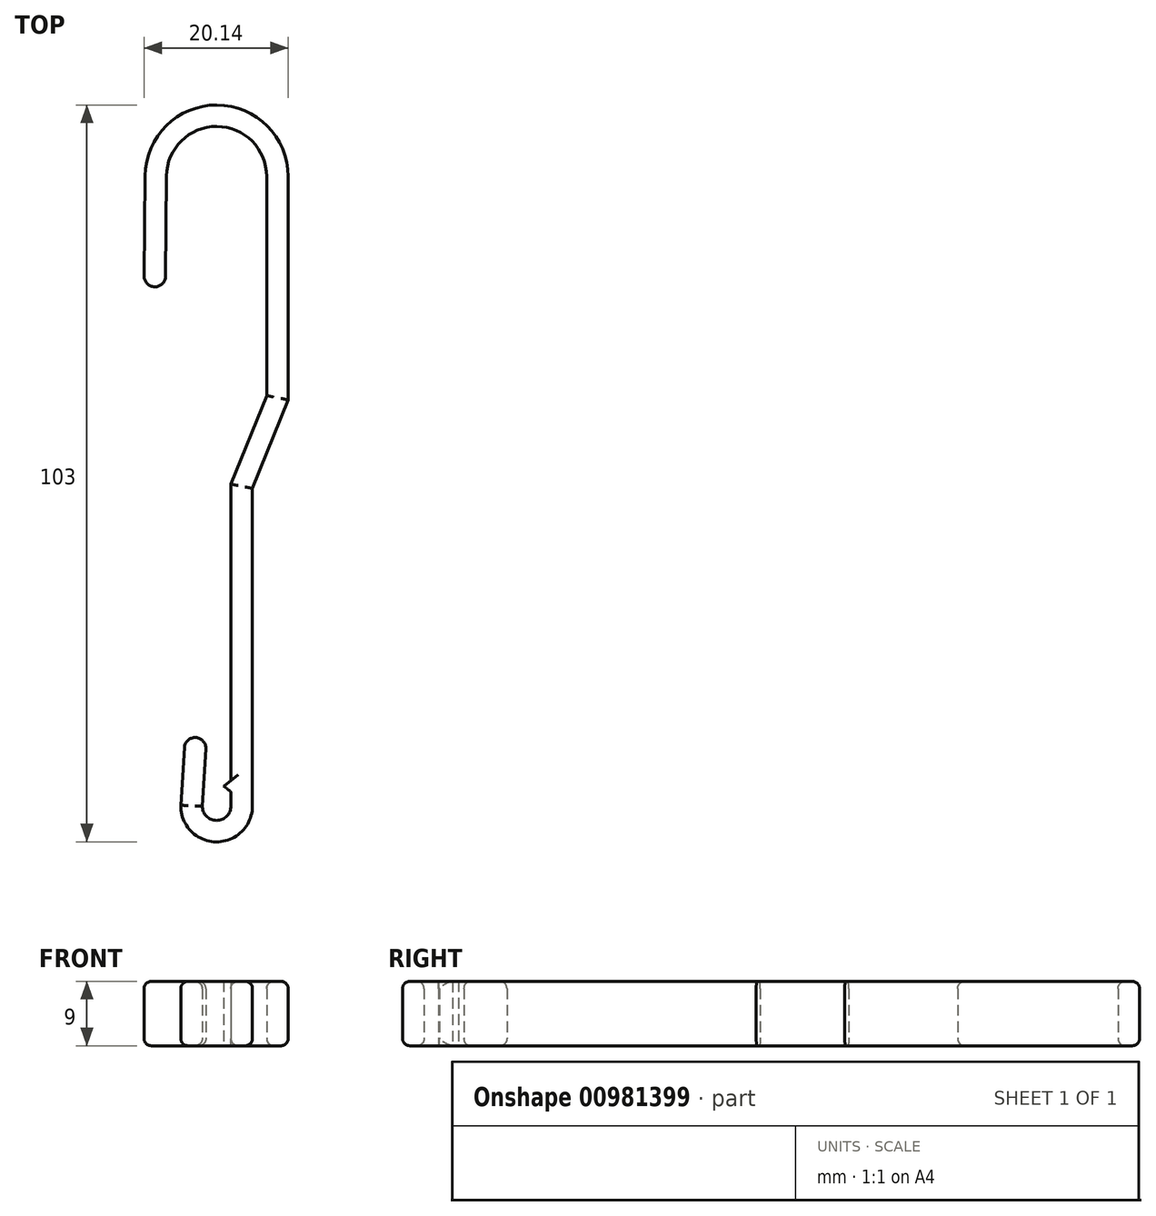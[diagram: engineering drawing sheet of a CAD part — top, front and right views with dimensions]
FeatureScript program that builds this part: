
annotation { "Feature Type Name" : "Feature", "Feature Type Description" : "" }
export const myFeature = defineFeature(function(context is Context, id is Id, definition is map)
    precondition{}
    {
        {
            var Q0;
            Q0=qCreatedBy(makeId("Top.planeOp"),FACE);
            var sketch = newSketch(context, id + "F0", { "sketchPlane" : qUnion([Q0])});
            skArc(sketch, "E0", {"start": v(-2, 0) * mm, "mid": v(0, -2) * mm, "end": v(2, 0) * mm});
            skLineSegment(sketch, "E1", {"start": v(-2, 0) * mm, "end": v(-1.5, 7.98) * mm});
            skLineSegment(sketch, "E2", {"start": v(2, 2) * mm, "end": v(1, 2.8) * mm});
            skLineSegment(sketch, "E3", {"start": v(1, 2.8) * mm, "end": v(2, 3.6) * mm});
            skLineSegment(sketch, "E4", {"start": v(2, 0) * mm, "end": v(2, 2) * mm});
            skLineSegment(sketch, "E5", {"start": v(2, 3.6) * mm, "end": v(2, 45) * mm});
            skArc(sketch, "E6", {"start": v(7, 88) * mm, "mid": v(0.03, 95) * mm, "end": v(-7, 88.07) * mm});
            skLineSegment(sketch, "E7", {"start": v(7, 88) * mm, "end": v(7, 57.38) * mm});
            skLineSegment(sketch, "E8", {"start": v(2, 45) * mm, "end": v(7, 57.38) * mm});
            skLineSegment(sketch, "E9", {"start": v(-7, 88.07) * mm, "end": v(-7.14, 74.07) * mm});
            skArc(sketch, "E10", {"start": v(-7.14, 74.07) * mm, "mid": v(-8.65, 72.58) * mm, "end": v(-10.14, 74.1) * mm});
            skLineSegment(sketch, "E11.0", {"start": v(-10, 88.1) * mm, "end": v(-10.14, 74.1) * mm});
            skLineSegment(sketch, "E11.1", {"start": v(5, 3.59) * mm, "end": v(5, 44.42) * mm});
            skLineSegment(sketch, "E11.2", {"start": v(5, 44.42) * mm, "end": v(10, 56.8) * mm});
            skLineSegment(sketch, "E11.3", {"start": v(10, 88) * mm, "end": v(10, 56.8) * mm});
            skArc(sketch, "E11.4", {"start": v(10, 88) * mm, "mid": v(0.05, 98) * mm, "end": v(-10, 88.1) * mm});
            skLineSegment(sketch, "E12.0", {"start": v(-5, 0.11) * mm, "end": v(-4.5, 8.17) * mm});
            skArc(sketch, "E12.1", {"start": v(-5, 0.11) * mm, "mid": v(-0.06, -5) * mm, "end": v(5, 0) * mm});
            skLineSegment(sketch, "E12.2", {"start": v(5, 0) * mm, "end": v(5, 2) * mm});
            skLineSegment(sketch, "E13", {"start": v(5, 2) * mm, "end": v(5, 3.59) * mm});
            skArc(sketch, "E14", {"start": v(-1.5, 7.98) * mm, "mid": v(-2.9, 9.58) * mm, "end": v(-4.5, 8.17) * mm});
            skSolve(sketch);
        }
        {
            var Q0;
            Q0 = qSketchRegion(id + "F0", true);
            extrude(context, id + "F1", {"entities" : qUnion([Q0]), "depth" : 9 * mm, "offsetDistance" : 25 * mm});
        }
        {
            var Q0;
            Q0=makeQuery(id+"F1.opExtrude","CAP_EDGE",EDGE,{"disambiguationData":[OSD([sQuery(id+"F0.wireOp",EDGE,"E11.1")])],"isStart":false});
            var Q1;
            Q1=makeQuery(id+"F1.opExtrude","CAP_EDGE",EDGE,{"disambiguationData":[OSD([sQuery(id+"F0.wireOp",EDGE,"E11.2")])],"isStart":false});
            var Q2;
            Q2=makeQuery(id+"F1.opExtrude","CAP_EDGE",EDGE,{"disambiguationData":[OSD([sQuery(id+"F0.wireOp",EDGE,"E11.3")])],"isStart":false});
            var Q3;
            Q3=makeQuery(id+"F1.opExtrude","CAP_EDGE",EDGE,{"disambiguationData":[OSD([sQuery(id+"F0.wireOp",EDGE,"E8")])],"isStart":false});
            var Q4;
            Q4=makeQuery(id+"F1.opExtrude","CAP_EDGE",EDGE,{"disambiguationData":[OSD([sQuery(id+"F0.wireOp",EDGE,"E5")])],"isStart":false});
            var Q5;
            Q5=makeQuery(id+"F1.opExtrude","CAP_EDGE",EDGE,{"disambiguationData":[OSD([sQuery(id+"F0.wireOp",EDGE,"E14")])],"isStart":false});
            var Q6;
            Q6=makeQuery(id+"F1.opExtrude","CAP_EDGE",EDGE,{"disambiguationData":[OSD([sQuery(id+"F0.wireOp",EDGE,"E12.0")])],"isStart":true});
            var Q7;
            Q7=makeQuery(id+"F1.opExtrude","CAP_EDGE",EDGE,{"disambiguationData":[OSD([sQuery(id+"F0.wireOp",EDGE,"E12.1")])],"isStart":true});
            var Q8;
            Q8=makeQuery(id+"F1.opExtrude","CAP_EDGE",EDGE,{"disambiguationData":[OSD([sQuery(id+"F0.wireOp",EDGE,"E5")])],"isStart":true});
            var Q9;
            Q9=makeQuery(id+"F1.opExtrude","CAP_EDGE",EDGE,{"disambiguationData":[OSD([sQuery(id+"F0.wireOp",EDGE,"E11.2")])],"isStart":true});
            var Q10;
            Q10=makeQuery(id+"F1.opExtrude","CAP_EDGE",EDGE,{"disambiguationData":[OSD([sQuery(id+"F0.wireOp",EDGE,"E11.3")])],"isStart":true});
            var Q11;
            Q11=makeQuery(id+"F1.opExtrude","CAP_EDGE",EDGE,{"disambiguationData":[OSD([sQuery(id+"F0.wireOp",EDGE,"E8")])],"isStart":true});
            fillet(context, id + "F2", {"entities" : qUnion([Q0, Q1, Q2, Q3, Q4, Q5, Q6, Q7, Q8, Q9, Q10, Q11]), "radius" : 1 * mm, "tangentPropagation" : true, "allowEdgeOverflow" : false});
        }
    });
